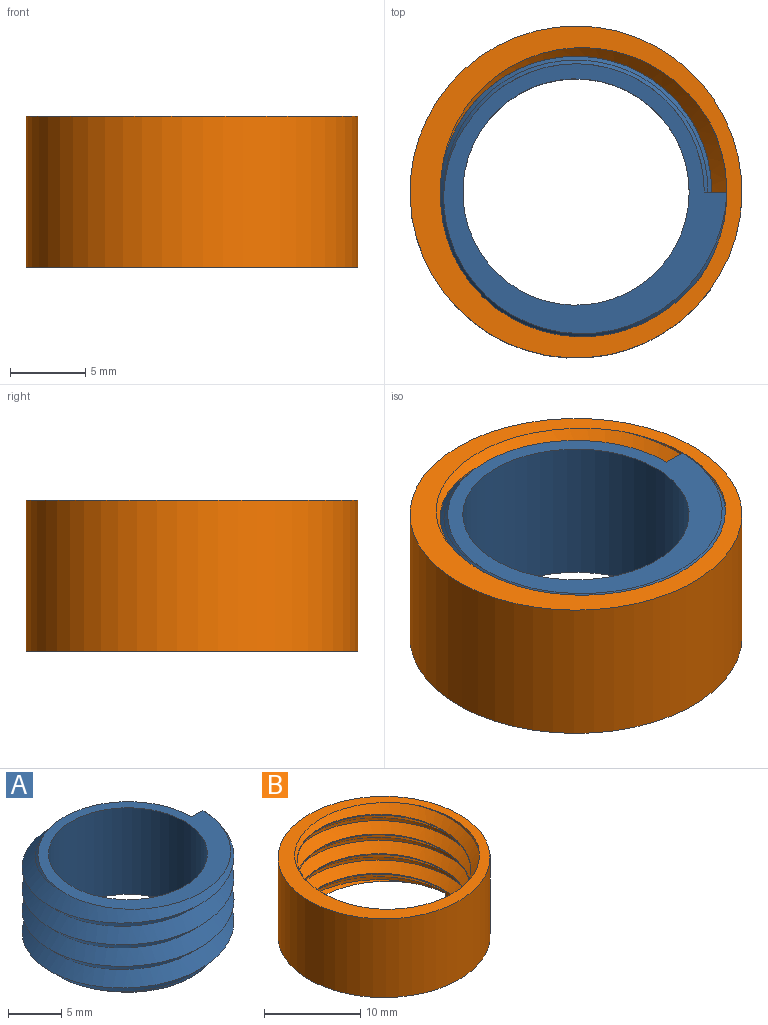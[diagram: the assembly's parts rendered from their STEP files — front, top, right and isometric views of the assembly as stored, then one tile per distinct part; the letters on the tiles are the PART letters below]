
ASSEMBLY  parts=2 mates=1
PART A: 11 faces, bbox 21x24.1x13.5 mm
  f0: plane 1.5x1.25mm, normal (0,1,0), area 1.1mm2, adj f1,f3,f6,f10
  f1: bspline ~17.5x10.1mm, area 8.7mm2, adj f0,f2,f3,f6
  f2: bspline ~23.09x20mm, area 391.6mm2, adj f1,f6,f8,f10
  f3: cylinder r=8.5mm len=15.4mm, axis (0,0,-1), area 10.7mm2, adj f0,f1,f6
  f4: cylinder r=7.5mm len=15mm, axis (0,0,-1), area 471.2mm2, adj f6,f7
  f5: cylinder r=8.5mm len=15.4mm, axis (0,0,-1), area 10.7mm2, adj f7,f8,f9
  f6: plane 19.81x18.93mm, normal (0,0,1), area 75.7mm2, adj f0,f1,f2,f3,f4
  f7: plane 19.8x18.92mm, normal (0,0,-1), area 75.7mm2, adj f4,f5,f8,f9,f10
  f8: plane 1.5x1.25mm, normal (0,-1,0), area 1.1mm2, adj f2,f5,f7,f9
  f9: bspline ~17.68x17.5mm, area 8.6mm2, adj f5,f7,f8,f10
  f10: bspline ~23.09x20mm, area 391.3mm2, adj f0,f2,f7,f9
PART B: 8 faces, bbox 22.7x23.8x13.1 mm
  f0: cylinder r=9mm len=18mm, axis (0,0,-1), area 38.5mm2, adj f1,f3,f4,f6,f7
  f1: plane 22.67x22.67mm, normal (0,0,-1), area 109.2mm2, adj f0,f2,f4,f5,f6
  f2: cylinder r=11mm len=22mm, axis (0,0,-1), area 691.2mm2, adj f1,f3
  f3: plane 22.67x22.67mm, normal (0,0,1), area 92.7mm2, adj f0,f2,f5,f6,f7
  f4: plane 1.2x1mm, normal (0,1,0), area 0.7mm2, adj f0,f1,f5,f7
  f5: cylinder r=10mm len=20mm, axis (0,0,1), area 112.8mm2, adj f1,f3,f4,f6,f7
  f6: bspline ~23.09x20mm, area 337.7mm2, adj f0,f1,f3,f5
  f7: bspline ~23.09x20mm, area 314mm2, adj f0,f3,f4,f5
PLACE A t=(17.56,3.66,17.85)mm
PLACE B rot(axis=(0,0,-1),1.6deg) t=(17.56,3.66,17.86)mm
MATE cylindrical A.f3 <-> B.f0  axis (0,0,-1) through (17.56,3.66,22.85)mm
